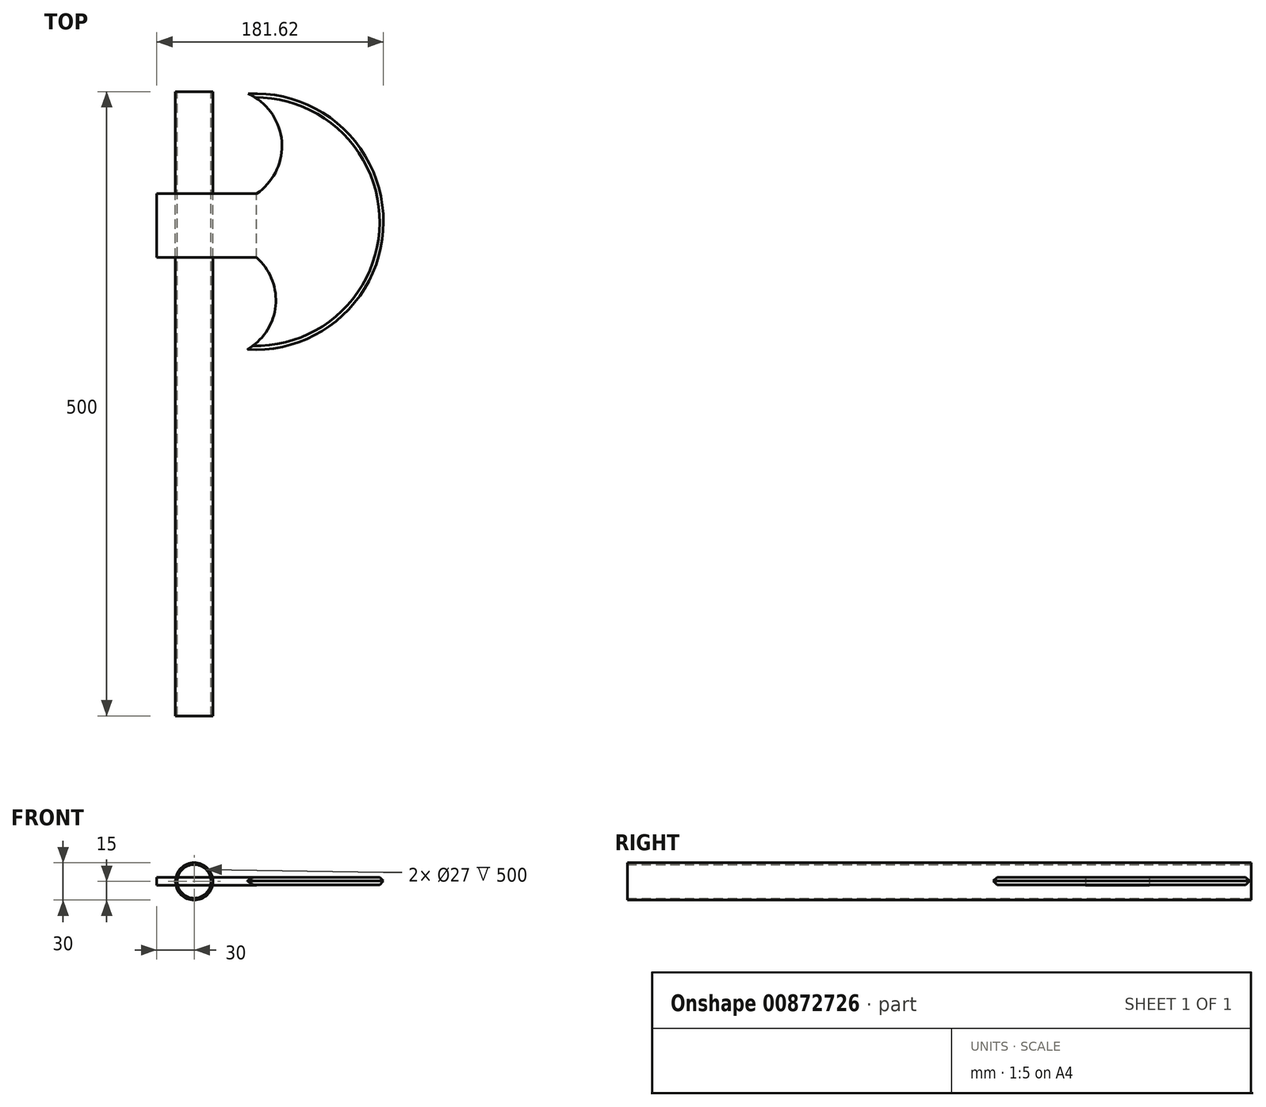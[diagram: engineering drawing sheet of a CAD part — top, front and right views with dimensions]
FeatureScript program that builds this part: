
annotation { "Feature Type Name" : "Feature", "Feature Type Description" : "" }
export const myFeature = defineFeature(function(context is Context, id is Id, definition is map)
    precondition{}
    {
        {
            var Q0;
            Q0=qCreatedBy(makeId("Front.planeOp"),FACE);
            var sketch = newSketch(context, id + "F0", { "sketchPlane" : qUnion([Q0])});
            skCircle(sketch, "E0", {"center": v(0, 0) * mm, "radius": 15 * mm});
            skCircle(sketch, "E1", {"center": v(0, 0) * mm, "radius": 13.5 * mm});
            skSolve(sketch);
        }
        {
            var Q0;
            Q0=makeQuery(id+"F0.imprint","IMPRINT",FACE,{"disambiguationData":[TD([[makeQuery(id+"F0.imprint","IMPRINT",EDGE,{"derivedFrom":sQuery(id+"F0.wireOp",EDGE,"E0")}),1.0]])]});
            extrude(context, id + "F1", {"entities" : qUnion([Q0]), "depth" : 500 * mm, "offsetDistance" : 25 * mm});
        }
        {
            var Q0;
            Q0=qCreatedBy(makeId("Right.planeOp"),FACE);
            var sketch = newSketch(context, id + "F2", { "sketchPlane" : qUnion([Q0])});
            skLineSegment(sketch, "E2.bottom", {"start": v(-132.8, 3.29) * mm, "end": v(-81.6, 3.29) * mm});
            skLineSegment(sketch, "E2.top", {"start": v(-132.8, -3.29) * mm, "end": v(-81.6, -3.29) * mm});
            skLineSegment(sketch, "E2.left", {"start": v(-132.8, 3.29) * mm, "end": v(-132.8, -3.29) * mm});
            skLineSegment(sketch, "E2.right", {"start": v(-81.6, 3.29) * mm, "end": v(-81.6, -3.29) * mm});
            skPoint(sketch, "E2.middle", {"position": v(-107.2, 0) * mm});
            skSolve(sketch);
        }
        {
            var Q0;
            Q0=makeQuery(id+"F2.imprint","IMPRINT",FACE,{"disambiguationData":[TD([[makeQuery(id+"F2.imprint","IMPRINT",EDGE,{"derivedFrom":sQuery(id+"F2.wireOp",EDGE,"E2.bottom")}),-1.0]])]});
            extrude(context, id + "F3", {"entities" : qUnion([Q0]), "depth" : 50 * mm, "offsetDistance" : 25 * mm, "hasSecondDirection" : true, "secondDirectionOppositeDirection" : true, "secondDirectionDepth" : 30 * mm});
        }
        {
            var Q0;
            Q0=makeQuery(id+"F3.opExtrude","SWEPT_FACE",FACE,{"disambiguationData":[OSD([sQuery(id+"F2.wireOp",EDGE,"E2.bottom")])]});
            var sketch = newSketch(context, id + "F4", { "sketchPlane" : qUnion([Q0])});
            skArc(sketch, "E3", {"start": v(50, -81.6) * mm, "mid": v(69.88, -37.44) * mm, "end": v(39.16, 0) * mm});
            skArc(sketch, "E4", {"start": v(39.16, -208.19) * mm, "mid": v(153.62, -104.1) * mm, "end": v(39.16, 0) * mm});
            skArc(sketch, "E5", {"start": v(39.16, -208.19) * mm, "mid": v(65, -173.43) * mm, "end": v(50, -132.8) * mm});
            skLineSegment(sketch, "E6", {"start": v(50, -81.6) * mm, "end": v(50, -132.8) * mm});
            skSolve(sketch);
        }
        {
            var Q0;
            Q0=makeQuery(id+"F4.imprint","IMPRINT",FACE,{"disambiguationData":[TD([[makeQuery(id+"F4.imprint","IMPRINT",EDGE,{"derivedFrom":sQuery(id+"F4.wireOp",EDGE,"E3")}),-1.0]])]});
            extrude(context, id + "F5", {"entities" : qUnion([Q0]), "operationType" : NewBodyOperationType.ADD, "oppositeDirection" : true, "depth" : 6 * mm, "offsetDistance" : 25 * mm});
        }
        {
            var Q0;
            Q0=makeQuery(id+"F5.opExtrude","CAP_EDGE",EDGE,{"disambiguationData":[OSD([sQuery(id+"F4.wireOp",EDGE,"E4")])],"isStart":false});
            var Q1;
            Q1=makeQuery(id+"F5.opExtrude","CAP_EDGE",EDGE,{"disambiguationData":[OSD([sQuery(id+"F4.wireOp",EDGE,"E4")])],"isStart":true});
            chamfer(context, id + "F6", {"entities" : qUnion([Q0, Q1]), "width" : 5 * mm, "tangentPropagation" : true});
        }
    });
